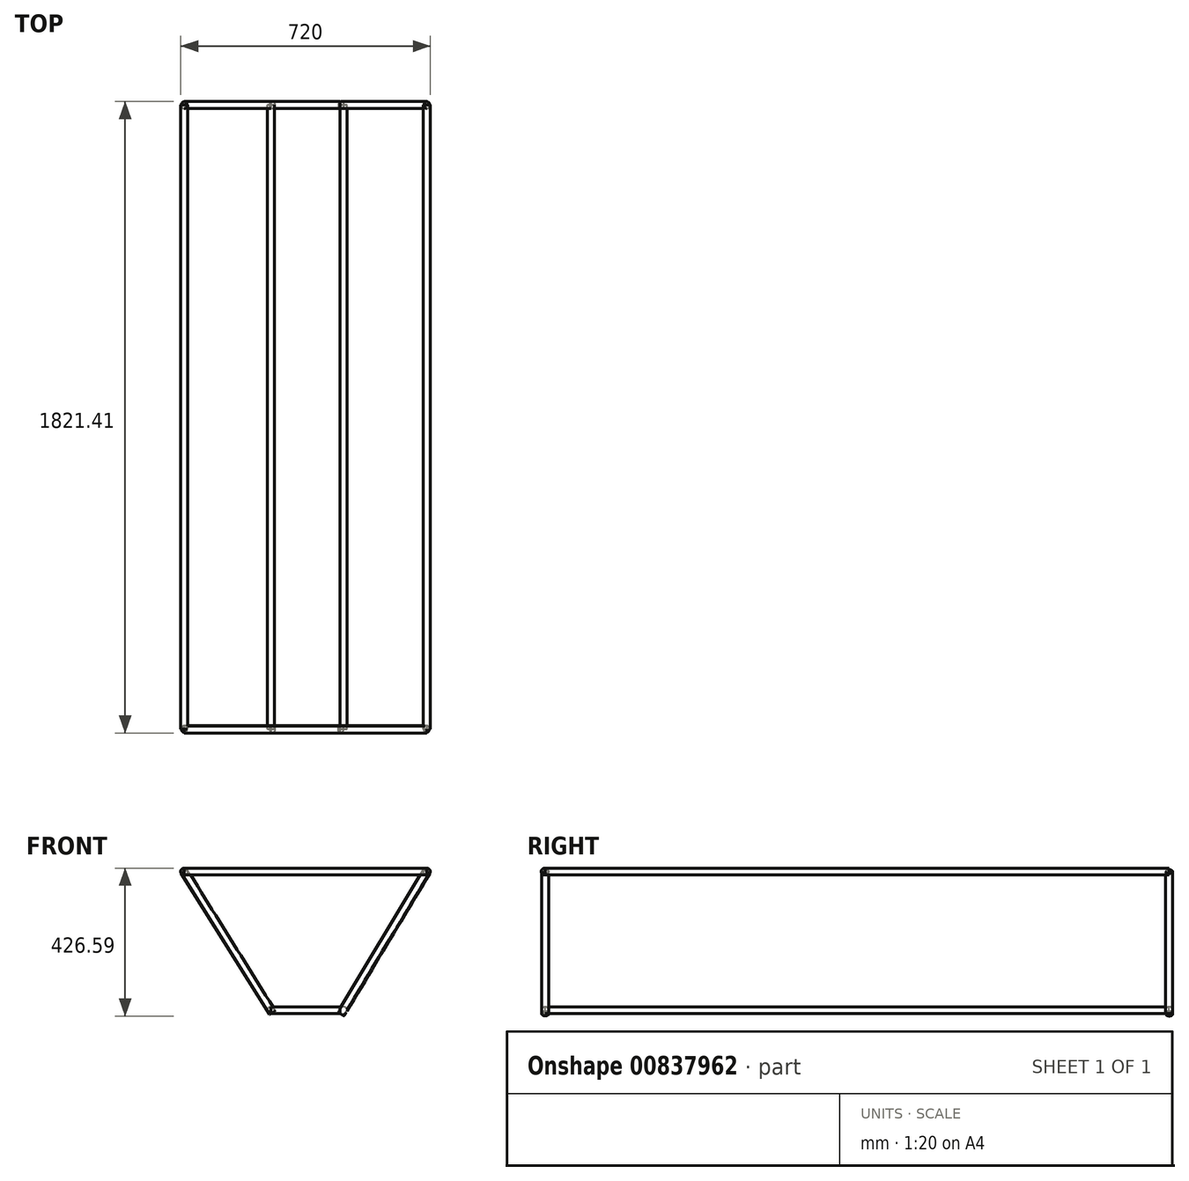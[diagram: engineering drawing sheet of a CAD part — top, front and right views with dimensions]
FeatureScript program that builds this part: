
annotation { "Feature Type Name" : "Feature", "Feature Type Description" : "" }
export const myFeature = defineFeature(function(context is Context, id is Id, definition is map)
    precondition{}
    {
        {
            var Q0;
            Q0=qCreatedBy(makeId("Front.planeOp"),FACE);
            var sketch = newSketch(context, id + "F0", { "sketchPlane" : qUnion([Q0])});
            skCircle(sketch, "E0", {"center": v(-350, 0) * mm, "radius": 10 * mm});
            skCircle(sketch, "E1", {"center": v(350, 0) * mm, "radius": 10 * mm});
            skPoint(sketch, "E2", {"position": v(0, -400) * mm});
            skCircle(sketch, "E3", {"center": v(110, -400) * mm, "radius": 10 * mm});
            skCircle(sketch, "E4", {"center": v(-100, -400) * mm, "radius": 10 * mm});
            skSolve(sketch);
        }
        {
            var Q0;
            Q0 = qSketchRegion(id + "F0", true);
            var Q1;
            Q1=makeQuery(id+"F0.imprint","IMPRINT",FACE,{"disambiguationData":[TD([[makeQuery(id+"F0.imprint","IMPRINT",EDGE,{"derivedFrom":sQuery(id+"F0.wireOp",EDGE,"E0")}),1.0]])]});
            extrude(context, id + "F1", {"entities" : qUnion([Q0, Q1]), "depth" : 1800 * mm, "offsetDistance" : 25 * mm});
        }
        {
            var Q0;
            Q0 = qSketchRegion(id + "F4", true);
            var Q1;
            Q1 = qSketchRegion(id + "F0", true);
            extrude(context, id + "F2", {"entities" : qUnion([Q0, Q1]), "operationType" : NewBodyOperationType.ADD, "depth" : 1800 * mm, "offsetDistance" : 25 * mm});
        }
        {
            var Q0;
            Q0 = qSketchRegion(id + "F0", true);
            extrude(context, id + "F3", {"entities" : qUnion([Q0]), "depth" : 1800 * mm, "offsetDistance" : 25 * mm});
        }
        {
            var Q0;
            Q0=qCreatedBy(makeId("Right.planeOp"),FACE);
            var sketch = newSketch(context, id + "F4", { "sketchPlane" : qUnion([Q0])});
            skCircle(sketch, "E5", {"center": v(0, 0) * mm, "radius": 10 * mm});
            skCircle(sketch, "E6", {"center": v(-1801.41, 0) * mm, "radius": 10 * mm});
            skCircle(sketch, "E7", {"center": v(0, -400.08) * mm, "radius": 10 * mm});
            skCircle(sketch, "E8", {"center": v(-1800.14, -400.08) * mm, "radius": 10 * mm});
            skSolve(sketch);
        }
        {
            var Q0;
            Q0=makeQuery(id+"F4.imprint","IMPRINT",FACE,{"disambiguationData":[TD([[makeQuery(id+"F4.imprint","IMPRINT",EDGE,{"derivedFrom":sQuery(id+"F4.wireOp",EDGE,"E7")}),1.0]])]});
            var Q1;
            Q1=makeQuery(id+"F4.imprint","IMPRINT",FACE,{"disambiguationData":[TD([[makeQuery(id+"F4.imprint","IMPRINT",EDGE,{"derivedFrom":sQuery(id+"F4.wireOp",EDGE,"E8")}),1.0]])]});
            extrude(context, id + "F5", {"entities" : qUnion([Q0, Q1]), "endBound" : BoundingType.SYMMETRIC, "depth" : 200 * mm, "offsetDistance" : 25 * mm});
        }
        {
            var Q0;
            Q0=makeQuery(id+"F4.imprint","IMPRINT",FACE,{"disambiguationData":[TD([[makeQuery(id+"F4.imprint","IMPRINT",EDGE,{"derivedFrom":sQuery(id+"F4.wireOp",EDGE,"E6")}),1.0]])]});
            extrude(context, id + "F6", {"entities" : qUnion([Q0]), "endBound" : BoundingType.SYMMETRIC, "depth" : 700 * mm, "offsetDistance" : 25 * mm});
        }
        {
            var Q0;
            Q0=sQuery(id+"F4.wireOp",EDGE,"E5");
            extrude(context, id + "F7", {"bodyType" : ToolBodyType.SURFACE, "surfaceEntities" : qUnion([Q0]), "endBound" : BoundingType.SYMMETRIC, "depth" : 700 * mm, "offsetDistance" : 25 * mm});
        }
        {
            var Q0;
            Q0=qCreatedBy(makeId("Top.planeOp"),FACE);
            var sketch = newSketch(context, id + "F8", { "sketchPlane" : qUnion([Q0])});
            skCircle(sketch, "E9", {"center": v(350, 0) * mm, "radius": 10 * mm});
            skCircle(sketch, "E10", {"center": v(-350, 0) * mm, "radius": 10 * mm});
            skCircle(sketch, "E11", {"center": v(-349.49, -1800.04) * mm, "radius": 10 * mm});
            skCircle(sketch, "E12", {"center": v(348.48, -1799.92) * mm, "radius": 10 * mm});
            skSolve(sketch);
        }
        {
            var Q0;
            Q0=makeQuery(id+"F8.imprint","IMPRINT",FACE,{"disambiguationData":[TD([[makeQuery(id+"F8.imprint","IMPRINT",EDGE,{"derivedFrom":sQuery(id+"F8.wireOp",EDGE,"E11")}),1.0]])]});
            var Q1;
            Q1=makeQuery(id+"F8.imprint","IMPRINT",FACE,{"disambiguationData":[TD([[makeQuery(id+"F8.imprint","IMPRINT",EDGE,{"derivedFrom":sQuery(id+"F8.wireOp",EDGE,"E12")}),1.0]])]});
            var Q2;
            Q2=makeQuery(id+"F8.imprint","IMPRINT",FACE,{"disambiguationData":[TD([[makeQuery(id+"F8.imprint","IMPRINT",EDGE,{"derivedFrom":sQuery(id+"F8.wireOp",EDGE,"E9")}),1.0]])]});
            var Q3;
            Q3=makeQuery(id+"F8.imprint","IMPRINT",FACE,{"disambiguationData":[TD([[makeQuery(id+"F8.imprint","IMPRINT",EDGE,{"derivedFrom":sQuery(id+"F8.wireOp",EDGE,"E10")}),1.0]])]});
            extrude(context, id + "F9", {"entities" : qUnion([Q0, Q1, Q2, Q3]), "oppositeDirection" : true, "depth" : 480 * mm, "offsetDistance" : 25 * mm});
        }
        {
            var Q0;
            Q0=makeQuery(id+"F9.opExtrude","SWEPT_BODY",BODY,{"disambiguationData":[OSD([sQuery(id+"F8.wireOp",EDGE,"E11")])]});
            var Q1;
            Q1=makeQuery(id+"F9.opExtrude","SWEPT_BODY",BODY,{"disambiguationData":[OSD([sQuery(id+"F8.wireOp",EDGE,"E10")])]});
            var Q2;
            Q2=makeQuery(id+"F1.opExtrude","SWEPT_FACE",FACE,{"disambiguationData":[OSD([sQuery(id+"F0.wireOp",EDGE,"E0")])]});
            transform(context, id + "F10", {"entities" : qUnion([Q0, Q1]), "transformType" : TransformType.ROTATION, "transformAxis" : qUnion([Q2]), "angle" : 32 * degree, "oppositeDirection" : true, "makeCopy" : false});
        }
        {
            var Q0;
            Q0=makeQuery(id+"F9.opExtrude","SWEPT_BODY",BODY,{"disambiguationData":[OSD([sQuery(id+"F8.wireOp",EDGE,"E12")])]});
            var Q1;
            Q1=makeQuery(id+"F9.opExtrude","SWEPT_BODY",BODY,{"disambiguationData":[OSD([sQuery(id+"F8.wireOp",EDGE,"E9")])]});
            var Q2;
            Q2=makeQuery(id+"F1.opExtrude","SWEPT_FACE",FACE,{"disambiguationData":[OSD([sQuery(id+"F0.wireOp",EDGE,"E1")])]});
            transform(context, id + "F11", {"entities" : qUnion([Q0, Q1]), "transformType" : TransformType.ROTATION, "transformAxis" : qUnion([Q2]), "angle" : 31 * degree, "makeCopy" : false});
        }
    });
